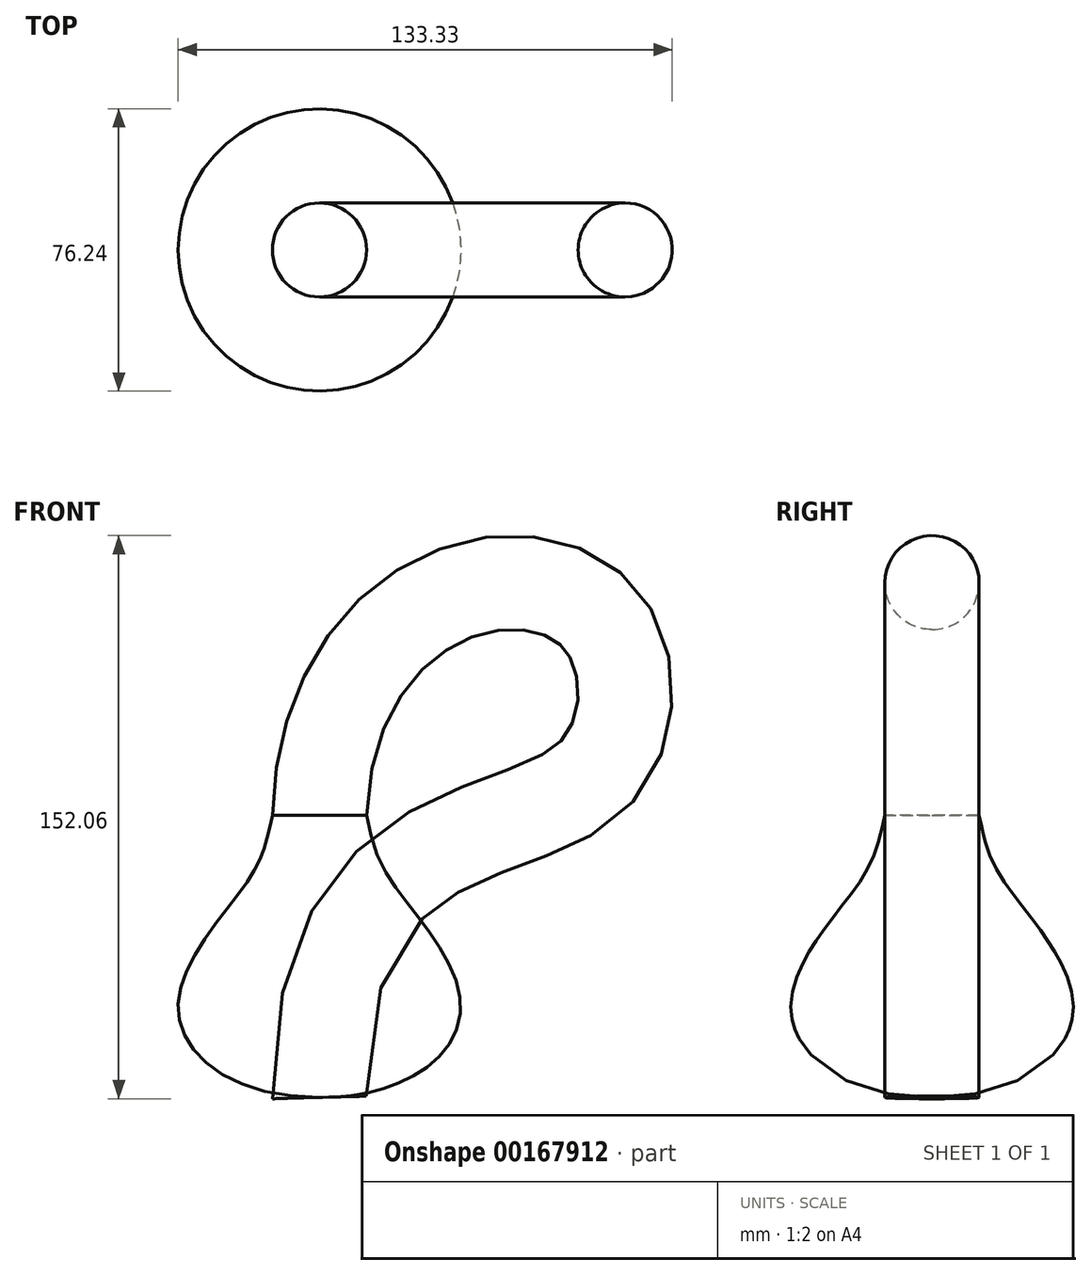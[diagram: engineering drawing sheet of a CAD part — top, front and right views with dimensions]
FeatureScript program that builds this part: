
annotation { "Feature Type Name" : "Feature", "Feature Type Description" : "" }
export const myFeature = defineFeature(function(context is Context, id is Id, definition is map)
    precondition{}
    {
        {
            var Q0;
            Q0=qCreatedBy(makeId("Front.planeOp"),FACE);
            var sketch = newSketch(context, id + "F0", { "sketchPlane" : qUnion([Q0])});
            skLineSegment(sketch, "E0", {"start": v(0, 0) * mm, "end": v(0, 25.4) * mm});
            skLineSegment(sketch, "E1", {"start": v(0, 25.4) * mm, "end": v(38.1, 25.4) * mm});
            skLineSegment(sketch, "E2", {"start": v(0, 25.4) * mm, "end": v(-38.1, 25.4) * mm});
            skLineSegment(sketch, "E3", {"start": v(0, 25.4) * mm, "end": v(0, 76.2) * mm});
            skLineSegment(sketch, "E4", {"start": v(-12.7, 76.2) * mm, "end": v(0, 76.2) * mm});
            skFitSpline(sketch, "E5", {"points": [v(-12.7, 76.2) * mm, v(-18.75, 59.36) * mm, v(-38.1, 25.4) * mm, v(0, 0) * mm], "startDerivative": vector(-18.67, -79.14) * mm, "endDerivative": vector(188.53, 0) * mm});
            skPoint(sketch, "E6.orphan", {"position": v(12.7, 76.2) * mm});
            skFitSpline(sketch, "E7", {"points": [v(0, 76.2) * mm, v(36.66, 136.16) * mm, v(76.76, 128.09) * mm, v(72.23, 85.42) * mm, v(0, 0) * mm], "startDerivative": vector(9.64, 360.18) * mm, "endDerivative": vector(0, -689.6) * mm});
            skSolve(sketch);
        }
        {
            var Q0;
            {var subQ0=sQuery(id+"F0.wireOp",EDGE,"E2");Q0=makeQuery(id+"F0.imprint","IMPRINT",FACE,{"disambiguationData":[TD([[makeQuery(id+"F0.imprint","IMPRINT",EDGE,{"derivedFrom":subQ0}),-1.0]])]});}
            var Q1;
            {var subQ0=sQuery(id+"F0.wireOp",EDGE,"E2");Q1=makeQuery(id+"F0.imprint","IMPRINT",FACE,{"disambiguationData":[TD([[makeQuery(id+"F0.imprint","IMPRINT",EDGE,{"derivedFrom":subQ0}),1.0]])]});}
            var Q2;
            Q2=sQuery(id+"F0.wireOp",EDGE,"E5");
            var Q3;
            Q3=sQuery(id+"F0.wireOp",EDGE,"E3");
            revolve(context, id + "F1", {"bodyType" : ToolBodyType.SURFACE, "entities" : qUnion([Q0, Q1]), "surfaceEntities" : qUnion([Q2]), "axis" : qUnion([Q3]), "revolveType" : RevolveType.FULL});
        }
        {
            var Q0;
            Q0=sQuery(id+"F0.wireOp",VERTEX,"E5.0.internal");
            var Q1;
            Q1=sQuery(id+"F0.wireOp",EDGE,"E3");
            cPlane(context, id + "F2", {"entities" : qUnion([Q0, Q1]), "cplaneType" : CPlaneType.LINE_POINT, "offset" : 25.4 * mm, "width" : 152.4 * mm, "height" : 152.4 * mm});
        }
        {
            var Q0;
            Q0=qCreatedBy(id+"F2.planeOp",FACE);
            var sketch = newSketch(context, id + "F3", { "sketchPlane" : qUnion([Q0])});
            skCircle(sketch, "E8", {"center": v(0, 0) * mm, "radius": 12.7 * mm});
            skSolve(sketch);
        }
        {
            var Q0;
            Q0=makeQuery(id+"F3.imprint","IMPRINT",FACE,{"disambiguationData":[TD([[makeQuery(id+"F3.imprint","IMPRINT",EDGE,{"derivedFrom":sQuery(id+"F3.wireOp",EDGE,"E8")}),1.0]])]});
            var Q1;
            Q1=sQuery(id+"F3.wireOp",EDGE,"E8");
            var Q2;
            Q2=sQuery(id+"F0.wireOp",EDGE,"E7");
            sweep(context, id + "F4", {"bodyType" : ToolBodyType.SURFACE, "operationType" : NewBodyOperationType.REMOVE, "profiles" : qUnion([Q0]), "surfaceProfiles" : qUnion([Q1]), "path" : qUnion([Q2])});
        }
    });
